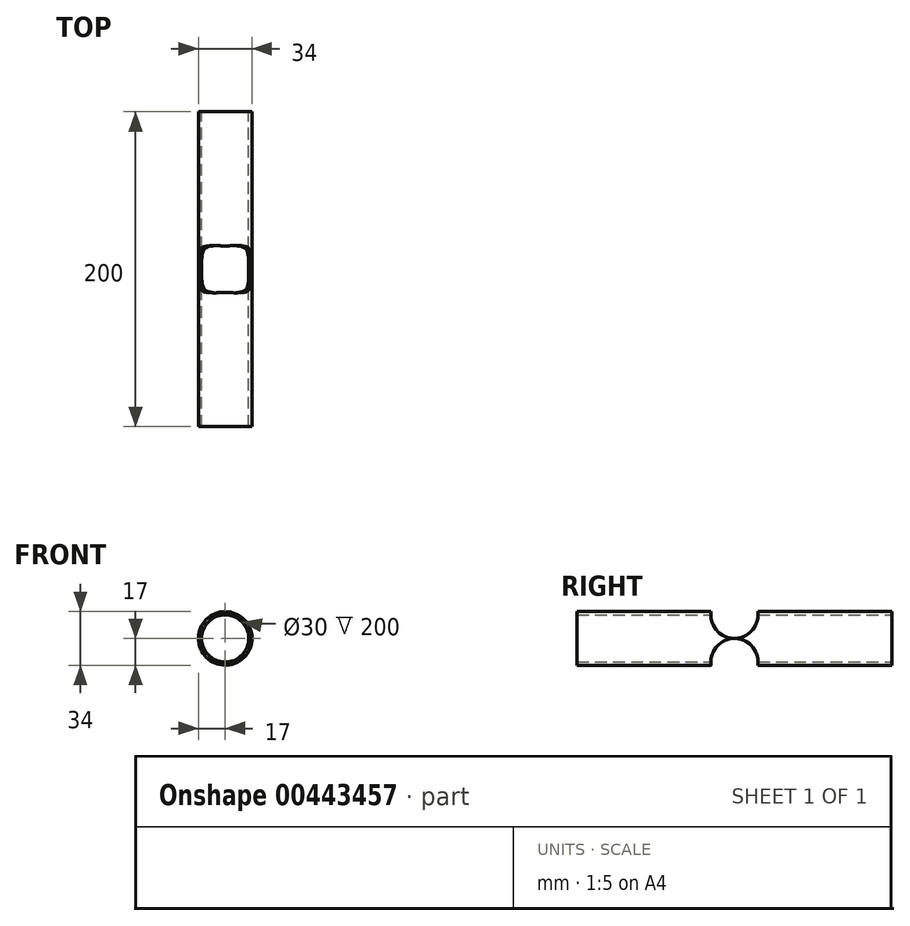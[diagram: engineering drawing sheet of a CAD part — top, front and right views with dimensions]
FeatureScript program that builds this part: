
annotation { "Feature Type Name" : "Feature", "Feature Type Description" : "" }
export const myFeature = defineFeature(function(context is Context, id is Id, definition is map)
    precondition{}
    {
        {
            var Q0;
            Q0=qCreatedBy(makeId("Front.planeOp"),FACE);
            var sketch = newSketch(context, id + "F0", { "sketchPlane" : qUnion([Q0])});
            skCircle(sketch, "E0", {"center": v(0, 0) * mm, "radius": 17 * mm});
            skCircle(sketch, "E1", {"center": v(0, 0) * mm, "radius": 15 * mm});
            skSolve(sketch);
        }
        {
            var Q0;
            Q0=makeQuery(id+"F0.imprint","IMPRINT",FACE,{"disambiguationData":[TD([[makeQuery(id+"F0.imprint","IMPRINT",EDGE,{"derivedFrom":sQuery(id+"F0.wireOp",EDGE,"E0")}),1.0]])]});
            extrude(context, id + "F1", {"entities" : qUnion([Q0]), "depth" : 200 * mm});
        }
        {
            var Q0;
            Q0=qCreatedBy(makeId("Right.planeOp"),FACE);
            var sketch = newSketch(context, id + "F2", { "sketchPlane" : qUnion([Q0])});
            skLineSegment(sketch, "E2", {"start": v(0, 0) * mm, "end": v(-100, 0) * mm, "construction": true});
            skLineSegment(sketch, "E3", {"start": v(-100, 0) * mm, "end": v(-100, 51.83) * mm, "construction": true});
            skLineSegment(sketch, "E4", {"start": v(-100, 0) * mm, "end": v(-100, -52.83) * mm, "construction": true});
            skCircle(sketch, "E5", {"center": v(-100, 15) * mm, "radius": 15 * mm});
            skCircle(sketch, "E6", {"center": v(-100, -15) * mm, "radius": 15 * mm});
            skSolve(sketch);
        }
        {
            var Q0;
            Q0=makeQuery(id+"F2.imprint","IMPRINT",FACE,{"disambiguationData":[TD([[makeQuery(id+"F2.imprint","IMPRINT",EDGE,{"derivedFrom":sQuery(id+"F2.wireOp",EDGE,"E5")}),1.0]])]});
            var Q1;
            Q1=makeQuery(id+"F2.imprint","IMPRINT",FACE,{"disambiguationData":[TD([[makeQuery(id+"F2.imprint","IMPRINT",EDGE,{"derivedFrom":sQuery(id+"F2.wireOp",EDGE,"E6")}),1.0]])]});
            var Q2;
            Q2=sQuery(id+"F2.wireOp",EDGE,"E5");
            var Q3;
            Q3=sQuery(id+"F2.wireOp",EDGE,"E6");
            extrude(context, id + "F3", {"entities" : qUnion([Q0, Q1]), "operationType" : NewBodyOperationType.REMOVE, "surfaceEntities" : qUnion([Q2, Q3]), "oppositeDirection" : true, "depth" : 25 * mm, "hasSecondDirection" : true, "secondDirectionOppositeDirection" : false, "secondDirectionDepth" : 25 * mm});
        }
    });
